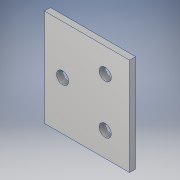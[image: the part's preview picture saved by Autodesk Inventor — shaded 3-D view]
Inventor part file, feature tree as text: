
AUTODESK INVENTOR PART (.ipt)
format: ipt  version: 2017 (Build 210142000, 142)  size: 147,968 bytes
history: native  units: in
note: dims shown in document units (in); Inventor stores cm internally (conversion verified against a paired STEP export)
features: sketch x4, hole x3, extrude x1, split x1
ambient origin geometry x8: Origin, YZ Plane, XZ Plane, XY Plane, X Axis, Y Axis, Z Axis, Center Point
bodies: Body1 (feature_tree)
feature tree (9):
  extrude  "Extrusion2"  Depth=0.5in
  hole  "Hole1"  [1 undecoded]
  hole  "Hole2"  [1 undecoded]
  hole  "Hole3"  [1 undecoded]
  split  "Split1"
  sketch  "Sketch3"  dims[d0=14.75in d3=0.5in]
  sketch  "Sketch4"  dims[d4=1.0in d5=0.25in]
  sketch  "Sketch5"  dims[d6=0.25in d10=0.25in]
  sketch  "Sketch6"  dims[d11=1.25in d12=0.125in d13=0.0in d14=0.9in d15=0.75in d16=0.375in d17=0.25in d18=0.5635in d19=1.0in d20=0.8108in d21=1.0in d22=0.25in d23=0.25in d24=0.75in d25=0.375in d26=0.25in d27=0.5635in d28=1.0in d29=0.8108in d30=3.689in d31=0.25in d32=0.75in d33=0.163in d34=0.75in d35=0.163in d36=0.163in d37=0.163in d38=0.75in d39=0.375in d40=0.25in d41=0.5635in d42=1.0in d43=0.8108in d44=0.5in]
note: 3 required parameter values undecoded (feature->parameter linkage not recoverable at this tier; creation-order binding heuristic only, values carry confidence <= 0.55)
